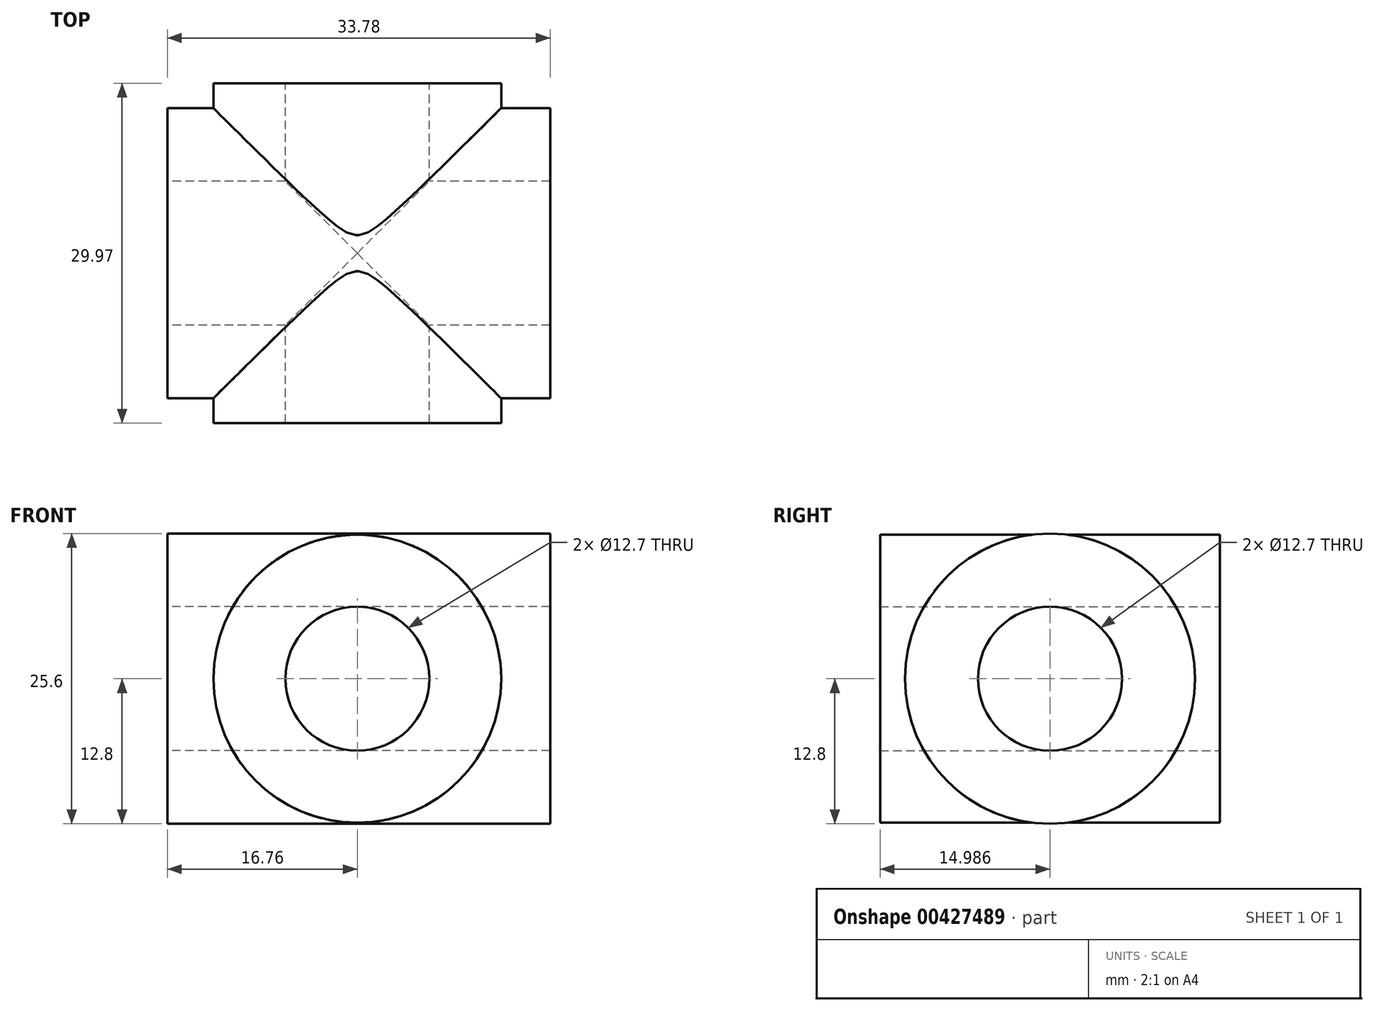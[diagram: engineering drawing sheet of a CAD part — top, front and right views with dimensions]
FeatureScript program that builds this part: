
annotation { "Feature Type Name" : "Feature", "Feature Type Description" : "" }
export const myFeature = defineFeature(function(context is Context, id is Id, definition is map)
    precondition{}
    {
        {
            var Q0;
            Q0=qCreatedBy(makeId("Front.planeOp"),FACE);
            var sketch = newSketch(context, id + "F0", { "sketchPlane" : qUnion([Q0])});
            skCircle(sketch, "E0", {"center": v(0, 0) * mm, "radius": 12.7 * mm});
            skSolve(sketch);
        }
        {
            var Q0;
            Q0 = qSketchRegion(id + "F0", true);
            extrude(context, id + "F1", {"entities" : qUnion([Q0]), "depth" : 29.97 * mm});
        }
        {
            var Q0;
            Q0=qCreatedBy(makeId("Right.planeOp"),FACE);
            var sketch = newSketch(context, id + "F2", { "sketchPlane" : qUnion([Q0])});
            skCircle(sketch, "E1", {"center": v(-14.98, 0) * mm, "radius": 12.8 * mm});
            skSolve(sketch);
        }
        {
            var Q0;
            Q0 = qSketchRegion(id + "F2", true);
            extrude(context, id + "F3", {"entities" : qUnion([Q0]), "operationType" : NewBodyOperationType.ADD, "oppositeDirection" : true, "depth" : 16.76 * mm, "hasSecondDirection" : true, "secondDirectionOppositeDirection" : false, "secondDirectionDepth" : 17.02 * mm});
        }
        {
            var Q0;
            Q0=makeQuery(id+"F1.opExtrude","CAP_FACE",FACE,{"disambiguationData":[OSD([sQuery(id+"F0.wireOp",EDGE,"E0")])],"isStart":true});
            var sketch = newSketch(context, id + "F4", { "sketchPlane" : qUnion([Q0])});
            skPoint(sketch, "E2", {"position": v(0, 0) * mm});
            skSolve(sketch);
        }
        {
            var Q0;
            Q0=sQuery(id+"F4.wireOp",VERTEX,"E2");
            var Q1;
            Q1=makeQuery(id+"F1.opExtrude","SWEPT_BODY",BODY,{"disambiguationData":[OSD([sQuery(id+"F0.wireOp",EDGE,"E0")])]});
            hole(context, id + "F5", {"style" : HoleStyle.SIMPLE, "endStyle" : HoleEndStyle.THROUGH, "holeDiameter" : 12.7 * mm, "isTappedThrough" : true, "tappedDepth" : 12.7 * mm, "tapClearance" : 3, "locations" : qUnion([Q0]), "scope" : qUnion([Q1])});
        }
        {
            var Q0;
            Q0=makeQuery(id+"F3.opExtrude","CAP_FACE",FACE,{"disambiguationData":[OSD([sQuery(id+"F2.wireOp",EDGE,"E1")])],"isStart":false});
            var sketch = newSketch(context, id + "F6", { "sketchPlane" : qUnion([Q0])});
            skPoint(sketch, "E3", {"position": v(14.98, 0) * mm});
            skSolve(sketch);
        }
        {
            var Q0;
            Q0=sQuery(id+"F6.wireOp",VERTEX,"E3");
            var Q1;
            Q1=makeQuery(id+"F1.opExtrude","SWEPT_BODY",BODY,{"disambiguationData":[OSD([sQuery(id+"F0.wireOp",EDGE,"E0")])]});
            hole(context, id + "F7", {"style" : HoleStyle.SIMPLE, "endStyle" : HoleEndStyle.THROUGH, "holeDiameter" : 12.7 * mm, "isTappedThrough" : true, "tappedDepth" : 12.7 * mm, "tapClearance" : 3, "locations" : qUnion([Q0]), "scope" : qUnion([Q1])});
        }
    });
